# Revit family: MPSHD
name_source: partatom
category: Communication Devices
revit_build: Autodesk Revit 2014 (Build: 20130308_1515(x64)
units: mm (PartAtom-declared; Revit-internal decimal feet)

## types (1)
- MPSHD
    Assembly Code = D5090
    Certification = UL and cUL Listed
    Default Elevation = 48 "
    Description = The MPS Auxiliary Pack is a self-contained transformer and relay (an ON/OFF switch
controlled by a circuit) designed for low-voltage 24VDC occupancy sensors.
    Features = Plenum rated • Self-contained relay • MPSA uses electrically held normally open relay • MPSHD uses robust latching relay provides unsurpassed and unrestricted performance • 100-277VAC, 50/60Hz • Regulated 24 VDC current; 100 mA output • Easily mounts inside or outside a junction box; inside a fixture • UL and cUL listed • Five-year limited warranty • Manual On available in MPSHD model • Power Indicator light in MPSHD model • Zero Arc Point Switching
    Housing Material = Paint - Hubbell - Carbon Black
    L = 5.3 "
    Manufacturer = Hubbell Control Solutions
    Model = MPSHD
    Product Documentation Link = https://hubbellcdn.com
    Product Page URL = https://www.hubbell.com
    Type Comments = Power Packs and Relays
    URL = https://www.hubbell.com
    Warranty = 5-Years Warranty
    Washer = Metal-Hubbell-Galvanized_Steel

## geometry (parser evidence)
native form markers: Sweep x1
no freeform markers — native parametric forms only
